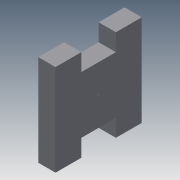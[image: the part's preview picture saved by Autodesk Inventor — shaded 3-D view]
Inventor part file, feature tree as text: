
AUTODESK INVENTOR PART (.ipt)
format: ipt  version: 2013 (Build 170138000, 138)  size: 91,136 bytes
history: native  units: mm
features: sketch x5, extrude x1, hole x1
ambient origin geometry x8: Origin, YZ Plane, XZ Plane, XY Plane, X Axis, Y Axis, Z Axis, Center Point
bodies: Solid1 (feature_tree)
feature tree (7):
  sketch  "Sketch1"  dims[d0=50.0mm d1=53.0mm]
  sketch  "Sketch2"  dims[d2=15.0mm d3=10.0mm]
  extrude  "Extrusion1"  Depth=53.0mm
  sketch  "Sketch4"  dims[d5=10.0mm]
  hole  "Hole1"  [1 undecoded]
  sketch  "Sketch3"  dims[d4=20.0mm]
  sketch  "Sketch5"  dims[d6=15.0mm d7=10.0mm d8=20.0mm d9=10.0mm d10=15.0mm d11=10.0mm d12=0.0mm d13=0.4mm d14=0.4mm d15=6.0mm d16=4.0mm d17=2.0mm d18=90.0deg d19=10.0mm d20=0.0mm]
note: 1 required parameter value undecoded (feature->parameter linkage not recoverable at this tier; creation-order binding heuristic only, values carry confidence <= 0.55)
